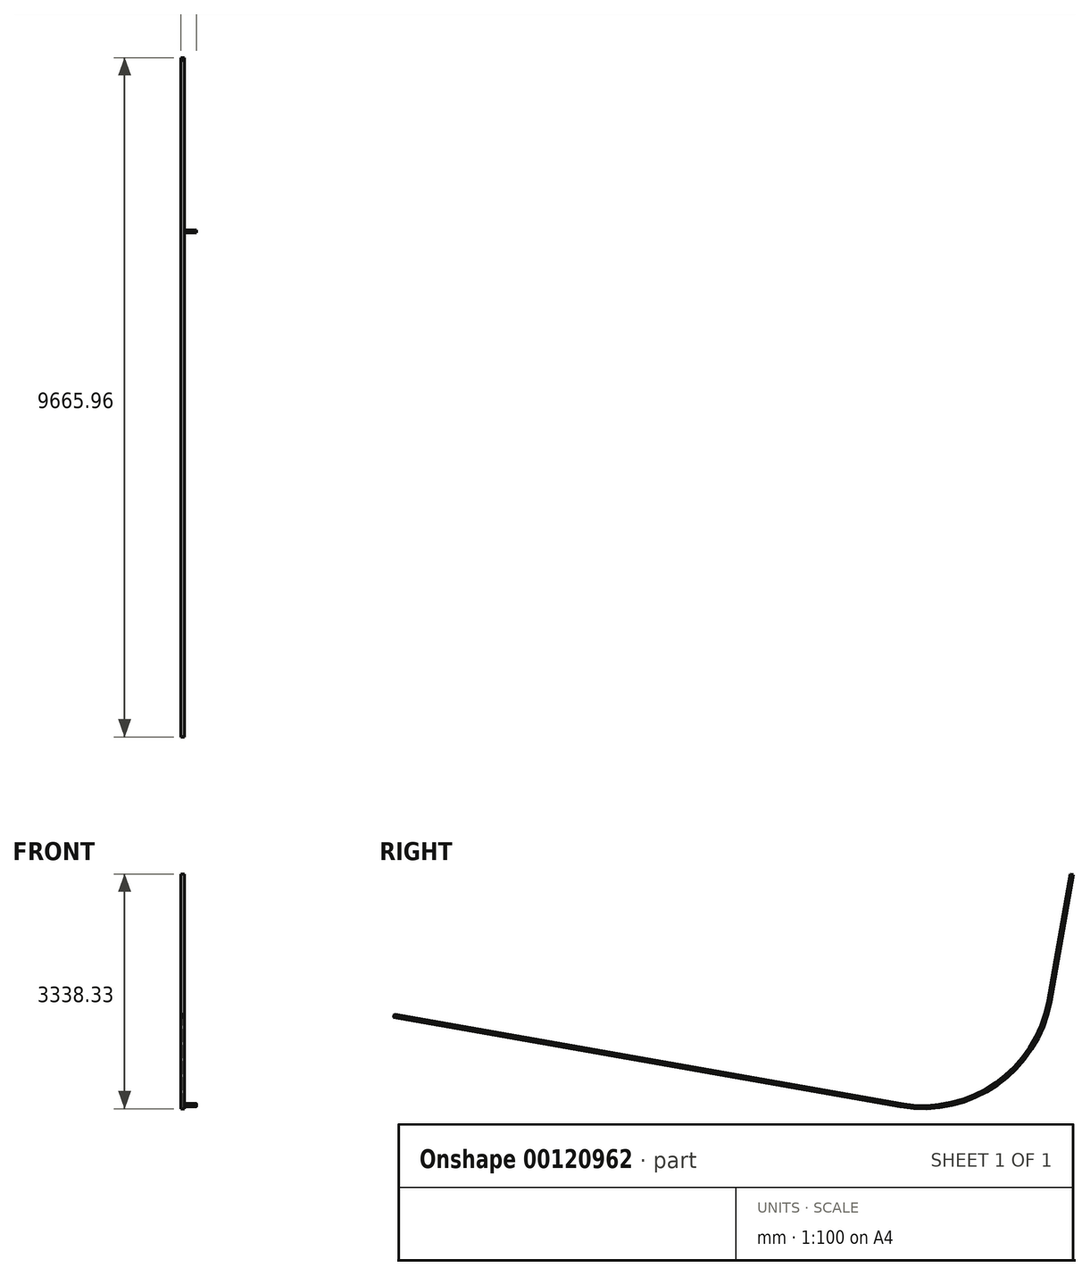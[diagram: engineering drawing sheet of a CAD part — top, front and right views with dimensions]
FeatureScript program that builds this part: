
annotation { "Feature Type Name" : "Feature", "Feature Type Description" : "" }
export const myFeature = defineFeature(function(context is Context, id is Id, definition is map)
    precondition{}
    {
        {
            var Q0;
            Q0=qCreatedBy(makeId("Right.planeOp"),FACE);
            cPlane(context, id + "F0", {"entities" : qUnion([Q0]), "cplaneType" : CPlaneType.OFFSET, "offset" : 226.7 * mm, "width" : 152.4 * mm, "height" : 152.4 * mm});
        }
        {
            var Q0;
            Q0=qCreatedBy(makeId("Right.planeOp"),FACE);
            var sketch = newSketch(context, id + "F1", { "sketchPlane" : qUnion([Q0])});
            skLineSegment(sketch, "E0", {"start": v(317.57, 1801.02) * mm, "end": v(635.14, 3602.03) * mm});
            skLineSegment(sketch, "E1", {"start": v(-1801.02, 317.57) * mm, "end": v(-9005.08, 1587.84) * mm});
            skLineSegment(sketch, "E2", {"start": v(0, 0) * mm, "end": v(635.14, 0) * mm, "construction": true});
            skArc(sketch, "E3", {"start": v(-1801.02, 317.57) * mm, "mid": v(-434.5, 620.52) * mm, "end": v(317.57, 1801.02) * mm});
            skLineSegment(sketch, "E4", {"start": v(317.57, 1801.02) * mm, "end": v(0, 0) * mm, "construction": true});
            skLineSegment(sketch, "E5", {"start": v(-1801.02, 317.57) * mm, "end": v(0, 0) * mm, "construction": true});
            skLineSegment(sketch, "E6", {"start": v(0, 0) * mm, "end": v(-9005.08, 0) * mm, "construction": true});
            skSolve(sketch);
        }
        {
            var Q0;
            Q0=sQuery(id+"F1.wireOp",VERTEX,"E0.end");
            var Q1;
            Q1=sQuery(id+"F1.wireOp",EDGE,"E0");
            cPlane(context, id + "F2", {"entities" : qUnion([Q0, Q1]), "cplaneType" : CPlaneType.LINE_POINT, "offset" : 25.4 * mm, "width" : 152.4 * mm, "height" : 152.4 * mm});
        }
        {
            var Q0;
            Q0=qCreatedBy(id+"F2.planeOp",FACE);
            var sketch = newSketch(context, id + "F3", { "sketchPlane" : qUnion([Q0])});
            skLineSegment(sketch, "E7.bottom", {"start": v(0, -17.46) * mm, "end": v(38.1, -17.46) * mm});
            skLineSegment(sketch, "E7.top", {"start": v(0, 17.46) * mm, "end": v(38.1, 17.46) * mm});
            skLineSegment(sketch, "E7.left", {"start": v(0, -17.46) * mm, "end": v(0, 17.46) * mm});
            skLineSegment(sketch, "E7.right", {"start": v(38.1, -17.46) * mm, "end": v(38.1, 17.46) * mm});
            skPoint(sketch, "E7.middle", {"position": v(19.05, 0) * mm});
            skLineSegment(sketch, "E8.bottom", {"start": v(0, -17.46) * mm, "end": v(50.8, -17.46) * mm});
            skLineSegment(sketch, "E8.top", {"start": v(0, -22.23) * mm, "end": v(50.8, -22.23) * mm});
            skLineSegment(sketch, "E8.left", {"start": v(0, -17.46) * mm, "end": v(0, -22.23) * mm});
            skLineSegment(sketch, "E8.right", {"start": v(50.8, -17.46) * mm, "end": v(50.8, -22.23) * mm});
            skLineSegment(sketch, "E9.bottom", {"start": v(0, 17.46) * mm, "end": v(50.8, 17.46) * mm});
            skLineSegment(sketch, "E9.top", {"start": v(0, 22.23) * mm, "end": v(50.8, 22.23) * mm});
            skLineSegment(sketch, "E9.left", {"start": v(0, 17.46) * mm, "end": v(0, 22.23) * mm});
            skLineSegment(sketch, "E9.right", {"start": v(50.8, 17.46) * mm, "end": v(50.8, 22.23) * mm});
            skSolve(sketch);
        }
        {
            var Q0;
            Q0=makeQuery(id+"F3.imprint","IMPRINT",FACE,{"disambiguationData":[TD([[makeQuery(id+"F3.imprint","IMPRINT",EDGE,{"derivedFrom":sQuery(id+"F3.wireOp",EDGE,"E7.bottom")}),1.0]])]});
            var Q1;
            Q1=makeQuery(id+"F3.imprint","IMPRINT",FACE,{"disambiguationData":[TD([[makeQuery(id+"F3.imprint","IMPRINT",EDGE,{"derivedFrom":sQuery(id+"F3.wireOp",EDGE,"E7.bottom")}),-1.0]])]});
            var Q2;
            Q2=makeQuery(id+"F3.imprint","IMPRINT",FACE,{"disambiguationData":[TD([[makeQuery(id+"F3.imprint","IMPRINT",EDGE,{"derivedFrom":sQuery(id+"F3.wireOp",EDGE,"E7.top")}),1.0]])]});
            var Q3;
            Q3=sQuery(id+"F1.wireOp",EDGE,"E0");
            var Q4;
            Q4=sQuery(id+"F1.wireOp",EDGE,"E3");
            var Q5;
            Q5=sQuery(id+"F1.wireOp",EDGE,"E1");
            sweep(context, id + "F4", {"profiles" : qUnion([Q0, Q1, Q2]), "path" : qUnion([Q3, Q4, Q5])});
        }
        {
            var Q0;
            Q0=makeQuery(id+"F4.opSweep","SWEPT_FACE",FACE,{"disambiguationData":[OSD([sQuery(id+"F1.wireOp",EDGE,"E0"),sQuery(id+"F3.wireOp",EDGE,"E7.right")])]});
            var sketch = newSketch(context, id + "F5", { "sketchPlane" : qUnion([Q0])});
            skLineSegment(sketch, "E10", {"start": v(-1797.98, 334.76) * mm, "end": v(-1804.05, 300.37) * mm, "construction": true});
            skLineSegment(sketch, "E11.0", {"start": v(-1804.88, 295.68) * mm, "end": v(-9008.94, 1565.95) * mm});
            skLineSegment(sketch, "E12", {"start": v(-1797.98, 334.76) * mm, "end": v(-1835.5, 341.38) * mm});
            skLineSegment(sketch, "E13", {"start": v(-1797.98, 334.76) * mm, "end": v(-1804.6, 297.24) * mm});
            skLineSegment(sketch, "E14.0", {"start": v(-1804.33, 326.21) * mm, "end": v(-1808.46, 302.76) * mm});
            skLineSegment(sketch, "E14.1", {"start": v(-1808.2, 331.73) * mm, "end": v(-1831.64, 335.86) * mm});
            skLineSegment(sketch, "E15", {"start": v(-1835.5, 341.38) * mm, "end": v(-1835.5, 341.38) * mm});
            skPoint(sketch, "E16.visualSharp", {"position": v(-1836.33, 336.7) * mm});
            skArc(sketch, "E16.filletArc", {"start": v(-1835.5, 341.38) * mm, "mid": v(-1834.72, 337.82) * mm, "end": v(-1831.64, 335.86) * mm});
            skLineSegment(sketch, "E17", {"start": v(-1804.6, 297.24) * mm, "end": v(-1804.6, 297.24) * mm});
            skPoint(sketch, "E18.visualSharp", {"position": v(-1809.3, 298.07) * mm});
            skArc(sketch, "E18.filletArc", {"start": v(-1808.46, 302.76) * mm, "mid": v(-1807.67, 299.2) * mm, "end": v(-1804.6, 297.24) * mm});
            skPoint(sketch, "E19.visualSharp", {"position": v(-1803.5, 330.9) * mm});
            skArc(sketch, "E19.filletArc", {"start": v(-1804.33, 326.21) * mm, "mid": v(-1805.12, 329.77) * mm, "end": v(-1808.2, 331.73) * mm});
            skSolve(sketch);
        }
        {
            var Q0;
            {var subQ2=sQuery(id+"F5.wireOp",EDGE,"E12");Q0=makeQuery(id+"F5.imprint","IMPRINT",FACE,{"disambiguationData":[TD([[makeQuery(id+"F5.imprint","IMPRINT",EDGE,{"derivedFrom":subQ2}),1.0]])]});}
            var Q1;
            {var subQ0=sQuery(id+"F5.wireOp",EDGE,"E13");var subQ6=sQuery(id+"F5.wireOp",EDGE,"E18.filletArc");var subQ7=makeQuery(id+"F5.imprint","INTERSECT",VERTEX,{"derivedFrom":[subQ0,subQ6]});Q1=makeQuery(id+"F5.imprint","IMPRINT",FACE,{"disambiguationData":[TD([[makeQuery(id+"F5.imprint","IMPRINT",EDGE,{"disambiguationData":[TD([[subQ7,1.0]])],"derivedFrom":subQ6}),1.0]])]});}
            var Q2;
            Q2=qCreatedBy(id+"F0.planeOp",FACE);
            extrude(context, id + "F6", {"entities" : qUnion([Q0, Q1]), "endBound" : BoundingType.UP_TO_SURFACE, "depth" : 25.4 * mm, "endBoundEntityFace" : qUnion([Q2]), "offsetDistance" : 25.4 * mm});
        }
        {
            var Q0;
            Q0=makeQuery(id+"F4.opSweep","SWEPT_BODY",BODY,{"disambiguationData":[OSD([sQuery(id+"F1.wireOp",EDGE,"E1"),sQuery(id+"F3.wireOp",EDGE,"E7.left"),sQuery(id+"F3.wireOp",EDGE,"E7.right"),sQuery(id+"F3.wireOp",EDGE,"E8.bottom"),sQuery(id+"F3.wireOp",EDGE,"E8.top"),sQuery(id+"F3.wireOp",EDGE,"E8.left"),sQuery(id+"F3.wireOp",EDGE,"E8.right"),sQuery(id+"F3.wireOp",EDGE,"E9.bottom"),sQuery(id+"F3.wireOp",EDGE,"E9.top"),sQuery(id+"F3.wireOp",EDGE,"E9.left"),sQuery(id+"F3.wireOp",EDGE,"E9.right")])]});
            var Q1;
            Q1=makeQuery(id+"F6.opExtrude","SWEPT_BODY",BODY,{"disambiguationData":[OSD([sQuery(id+"F5.wireOp",EDGE,"E12"),sQuery(id+"F5.wireOp",EDGE,"E13"),sQuery(id+"F5.wireOp",EDGE,"E14.0"),sQuery(id+"F5.wireOp",EDGE,"E14.1"),sQuery(id+"F5.wireOp",EDGE,"E16.filletArc"),sQuery(id+"F5.wireOp",EDGE,"E18.filletArc"),sQuery(id+"F5.wireOp",EDGE,"E19.filletArc")])]});
            booleanBodies(context, id + "F7", {"operationType" : BooleanOperationType.SUBTRACTION, "tools" : qUnion([Q0]), "targets" : qUnion([Q1]), "keepTools" : true});
        }
    });
